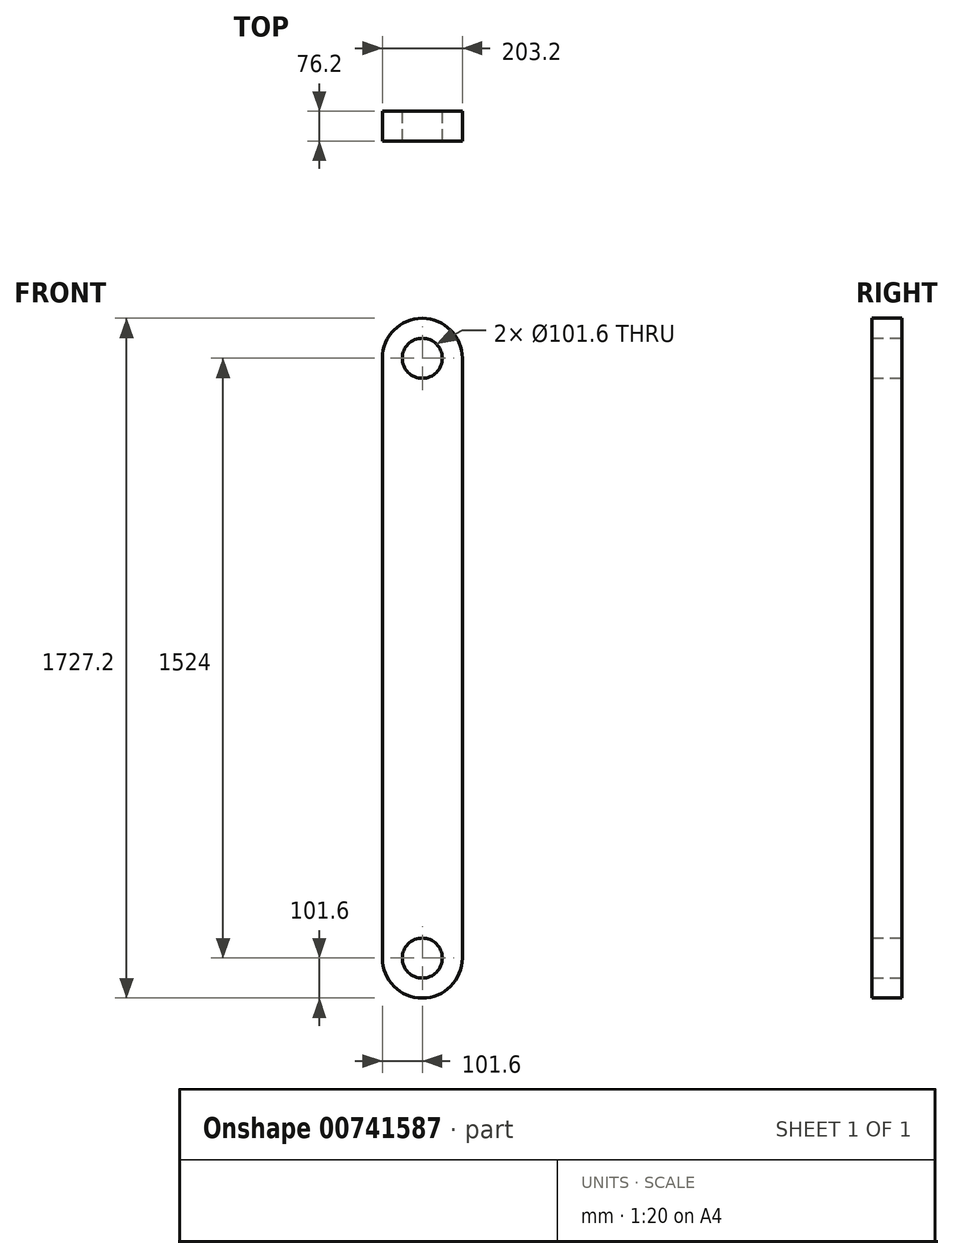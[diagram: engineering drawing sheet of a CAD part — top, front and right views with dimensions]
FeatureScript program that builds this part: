
annotation { "Feature Type Name" : "Feature", "Feature Type Description" : "" }
export const myFeature = defineFeature(function(context is Context, id is Id, definition is map)
    precondition{}
    {
        {
            var Q0;
            Q0=qCreatedBy(makeId("Front.planeOp"),FACE);
            var sketch = newSketch(context, id + "F0", { "sketchPlane" : qUnion([Q0])});
            skLineSegment(sketch, "E0.bottom", {"start": v(0, -101.6) * mm, "end": v(0, -101.6) * mm});
            skLineSegment(sketch, "E0.top", {"start": v(0, 1625.6) * mm, "end": v(0, 1625.6) * mm});
            skLineSegment(sketch, "E0.left", {"start": v(-101.6, 0) * mm, "end": v(-101.6, 1524) * mm});
            skLineSegment(sketch, "E0.right", {"start": v(101.6, 0) * mm, "end": v(101.6, 1524) * mm});
            skPoint(sketch, "E1.visualSharp", {"position": v(-101.6, 1625.6) * mm});
            skArc(sketch, "E1.filletArc", {"start": v(0, 1625.6) * mm, "mid": v(-71.84, 1595.84) * mm, "end": v(-101.6, 1524) * mm});
            skPoint(sketch, "E2.visualSharp", {"position": v(-101.6, -101.6) * mm});
            skArc(sketch, "E2.filletArc", {"start": v(-101.6, 0) * mm, "mid": v(-71.84, -71.84) * mm, "end": v(0, -101.6) * mm});
            skPoint(sketch, "E3.visualSharp", {"position": v(101.6, -101.6) * mm});
            skArc(sketch, "E3.filletArc", {"start": v(0, -101.6) * mm, "mid": v(71.84, -71.84) * mm, "end": v(101.6, 0) * mm});
            skPoint(sketch, "E4.visualSharp", {"position": v(101.6, 1625.6) * mm});
            skArc(sketch, "E4.filletArc", {"start": v(101.6, 1524) * mm, "mid": v(71.84, 1595.84) * mm, "end": v(0, 1625.6) * mm});
            skCircle(sketch, "E5", {"center": v(0, 1524) * mm, "radius": 50.8 * mm});
            skCircle(sketch, "E6", {"center": v(0, 0) * mm, "radius": 50.8 * mm});
            skSolve(sketch);
        }
        {
            var Q0;
            Q0 = qSketchRegion(id + "F0", true);
            extrude(context, id + "F1", {"entities" : qUnion([Q0]), "depth" : 76.2 * mm, "offsetDistance" : 25.4 * mm});
        }
    });
